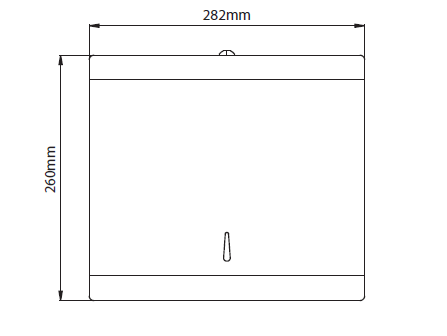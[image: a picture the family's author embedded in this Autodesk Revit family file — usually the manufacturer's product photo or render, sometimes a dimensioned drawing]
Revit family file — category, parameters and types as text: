
# Revit family: 706150001_Dispensador de Toallas
name_source: partatom
category: Plumbing Fixtures
units: mm (PartAtom-declared; Revit-internal decimal feet)

## family parameters
Always vertical = Yes
Cut with Voids When Loaded = No
Host = Wall
OmniClass Number = 23.21.43.15.25
OmniClass Title = Paper Towel Dispensers
Part Type = Normal
Room Calculation Point = No
Round Connector Dimension = Use Diameter
Shared = No

## types (1)
- Type 1
    Alto = 260 mm  [stored 0.853018 ft]
    Ancho = 282 mm
    Colección = Descarga Muro
    Creado por = BIMBAU
    Default Elevation = 0 mm  [stored 0 ft]
    Description = Compra hoy el dispensador de toallas con sistema antivandálico con llave, es la solución perfecta para espacios de alto tráfico, además está elaborado en acero inoxidable 304.
    Fecha de creación = 15/04/2021
    Garantía = 1 Año
    Garantía Acabados = 3 Años
    Línea = Accesorios Institucionales
    Manufacturer = Corona
    Material = Corona_Acero inoxidable
    Material 2 = Corona_Acero_Negro Mate
    Model = Dispensador de Toallas
    Profundidad = 102 mm  [stored 0.334646 ft]
    Referencia = 706150001
    Resistencia = Resistente a la corrosión pelado y decoloración por agua. Resistente al efecto de jabones y limpiadores de tocador
    Tipo de instalación = A pared
    URL = https://corona.co
    Uso = Institucional

note: [stored X ft] marks values corroborated as IEEE doubles in the binary element streams (Revit-internal decimal feet)

## geometry (parser evidence)
native form markers: Sweep x8
no freeform markers — native parametric forms only
